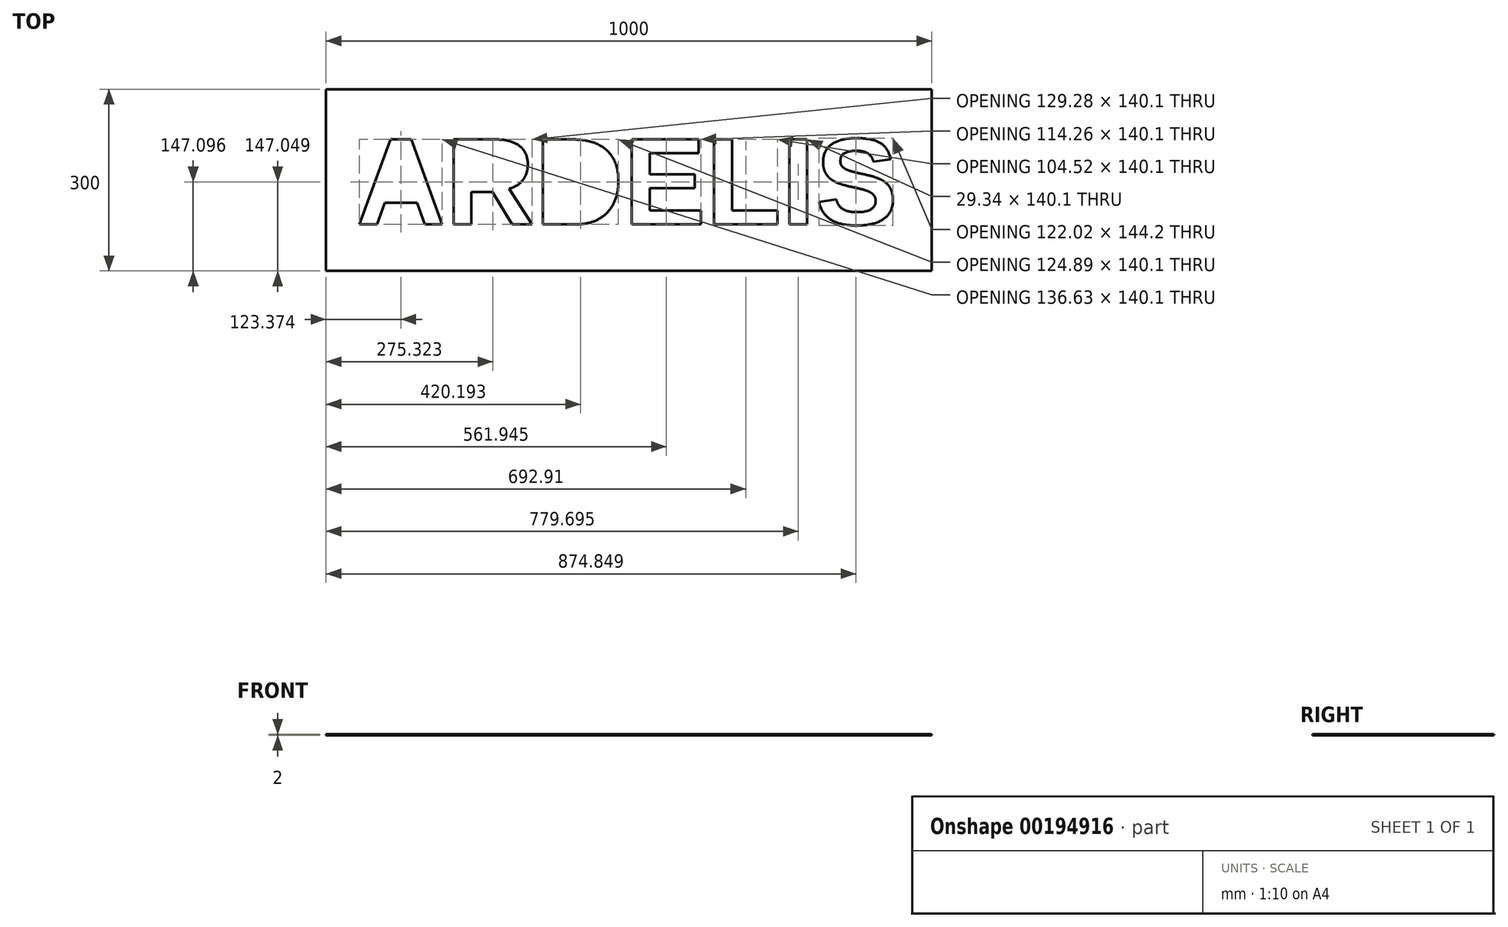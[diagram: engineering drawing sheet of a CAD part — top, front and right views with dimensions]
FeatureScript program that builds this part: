
annotation { "Feature Type Name" : "Feature", "Feature Type Description" : "" }
export const myFeature = defineFeature(function(context is Context, id is Id, definition is map)
    precondition{}
    {
        {
            var Q0;
            Q0=qCreatedBy(makeId("Top.planeOp"),FACE);
            var sketch = newSketch(context, id + "F0", { "sketchPlane" : qUnion([Q0])});
            skLineSegment(sketch, "E0.bottom", {"start": v(500, 150) * mm, "end": v(-500, 150) * mm});
            skLineSegment(sketch, "E0.top", {"start": v(500, -150) * mm, "end": v(-500, -150) * mm});
            skLineSegment(sketch, "E0.left", {"start": v(500, 150) * mm, "end": v(500, -150) * mm});
            skLineSegment(sketch, "E0.right", {"start": v(-500, 150) * mm, "end": v(-500, -150) * mm});
            skPoint(sketch, "E0.middle", {"position": v(0, 0) * mm});
            skText(sketch, "E1", { "text": "ARDELIS", "fontName": "Arimo-Bold.ttf"});
            const initialGuessF0  = {"E1": [-0.45, -0.073, 1, 0, 0.14662]};
            skSetInitialGuess(sketch, initialGuessF0);
            skSolve(sketch);
        }
        {
            var Q0;
            Q0 = qSketchRegion(id + "F0", true);
            extrude(context, id + "F1", {"entities" : qUnion([Q0]), "depth" : 2 * mm});
        }
    });
